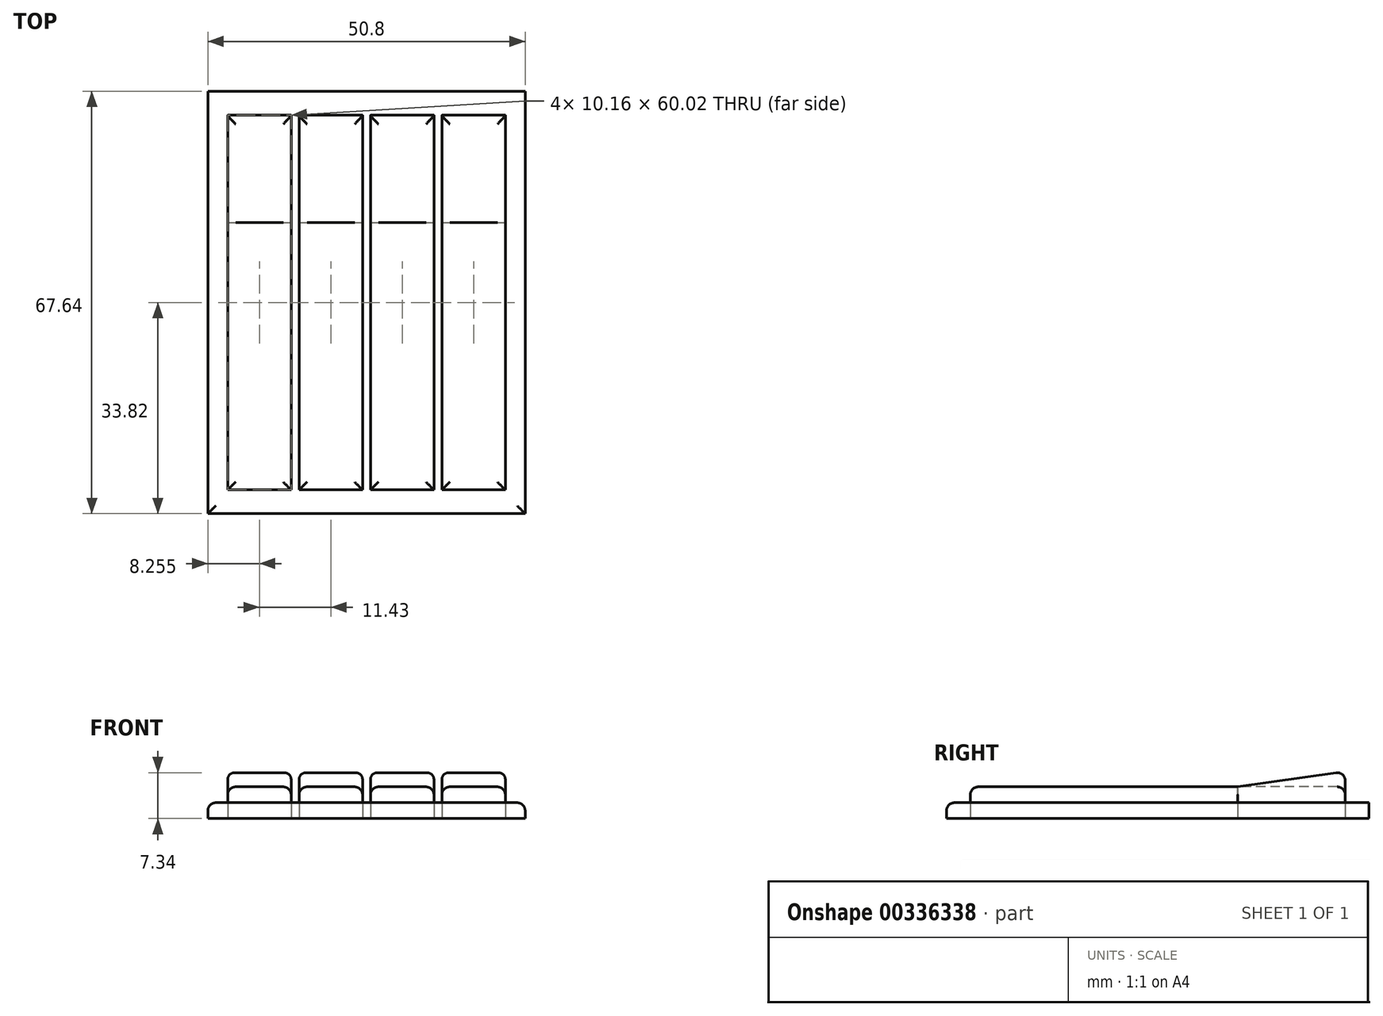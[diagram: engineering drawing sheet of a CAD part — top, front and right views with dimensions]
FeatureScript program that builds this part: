
annotation { "Feature Type Name" : "Feature", "Feature Type Description" : "" }
export const myFeature = defineFeature(function(context is Context, id is Id, definition is map)
    precondition{}
    {
        {
            var Q0;
            Q0=qCreatedBy(makeId("Top.planeOp"),FACE);
            var sketch = newSketch(context, id + "F0", { "sketchPlane" : qUnion([Q0])});
            skPoint(sketch, "E0.visualSharp", {"position": v(-51.01, 40.39) * mm});
            skPoint(sketch, "E1.visualSharp", {"position": v(51.07, 40.48) * mm});
            skPoint(sketch, "E2.visualSharp", {"position": v(0.11, -47.97) * mm});
            skLineSegment(sketch, "E3.bottom", {"start": v(25.4, 33.82) * mm, "end": v(-25.4, 33.82) * mm});
            skLineSegment(sketch, "E3.top", {"start": v(25.4, -33.82) * mm, "end": v(-25.4, -33.82) * mm});
            skLineSegment(sketch, "E3.left", {"start": v(25.4, 33.82) * mm, "end": v(25.4, -33.82) * mm});
            skLineSegment(sketch, "E3.right", {"start": v(-25.4, 33.82) * mm, "end": v(-25.4, -33.82) * mm});
            skPoint(sketch, "E3.middle", {"position": v(-17.14, 0) * mm});
            skLineSegment(sketch, "E4.bottom", {"start": v(-12.06, 30) * mm, "end": v(-22.22, 30) * mm});
            skLineSegment(sketch, "E4.top", {"start": v(-12.06, -30) * mm, "end": v(-22.22, -30) * mm});
            skLineSegment(sketch, "E4.left", {"start": v(-12.06, 30) * mm, "end": v(-12.06, -30) * mm});
            skLineSegment(sketch, "E4.right", {"start": v(-22.22, 30) * mm, "end": v(-22.22, -30) * mm});
            skPoint(sketch, "E5.1.0.0", {"position": v(-5.71, 0) * mm});
            skLineSegment(sketch, "E5.1.0.1", {"start": v(-0.63, -30) * mm, "end": v(-10.8, -30) * mm});
            skLineSegment(sketch, "E5.1.0.2", {"start": v(-0.63, 30) * mm, "end": v(-0.63, -30) * mm});
            skLineSegment(sketch, "E5.1.0.3", {"start": v(-10.8, 30) * mm, "end": v(-10.8, -30) * mm});
            skLineSegment(sketch, "E5.1.0.4", {"start": v(-0.63, 30) * mm, "end": v(-10.8, 30) * mm});
            skPoint(sketch, "E5.1.0.5", {"position": v(-5.71, 0) * mm});
            skPoint(sketch, "E5.2.0.0", {"position": v(5.72, 0) * mm});
            skLineSegment(sketch, "E5.2.0.1", {"start": v(10.8, -30) * mm, "end": v(0.64, -30) * mm});
            skLineSegment(sketch, "E5.2.0.2", {"start": v(10.8, 30) * mm, "end": v(10.8, -30) * mm});
            skLineSegment(sketch, "E5.2.0.3", {"start": v(0.64, 30) * mm, "end": v(0.64, -30) * mm});
            skLineSegment(sketch, "E5.2.0.4", {"start": v(10.8, 30) * mm, "end": v(0.64, 30) * mm});
            skPoint(sketch, "E5.2.0.5", {"position": v(5.72, 0) * mm});
            skPoint(sketch, "E5.3.0.0", {"position": v(17.15, 0) * mm});
            skLineSegment(sketch, "E5.3.0.1", {"start": v(22.23, -30) * mm, "end": v(12.07, -30) * mm});
            skLineSegment(sketch, "E5.3.0.2", {"start": v(22.23, 30) * mm, "end": v(22.23, -30) * mm});
            skLineSegment(sketch, "E5.3.0.3", {"start": v(12.07, 30) * mm, "end": v(12.07, -30) * mm});
            skLineSegment(sketch, "E5.3.0.4", {"start": v(22.23, 30) * mm, "end": v(12.07, 30) * mm});
            skPoint(sketch, "E5.3.0.5", {"position": v(17.15, 0) * mm});
            skLineSegment(sketch, "E5.direction1", {"start": v(-22.22, -30) * mm, "end": v(-10.8, -30) * mm, "construction": true});
            skLineSegment(sketch, "E6", {"start": v(-22.22, 12.8) * mm, "end": v(22.23, 12.8) * mm});
            skSolve(sketch);
        }
        {
            var Q0;
            {var subQ0=sQuery(id+"F0.wireOp",EDGE,"E4.bottom");Q0=makeQuery(id+"F0.imprint","IMPRINT",FACE,{"disambiguationData":[TD([[makeQuery(id+"F0.imprint","IMPRINT",EDGE,{"derivedFrom":subQ0}),1.0]])]});}
            var Q1;
            {var subQ0=sQuery(id+"F0.wireOp",EDGE,"E5.1.0.4");Q1=makeQuery(id+"F0.imprint","IMPRINT",FACE,{"disambiguationData":[TD([[makeQuery(id+"F0.imprint","IMPRINT",EDGE,{"derivedFrom":subQ0}),1.0]])]});}
            var Q2;
            {var subQ0=sQuery(id+"F0.wireOp",EDGE,"E5.2.0.4");Q2=makeQuery(id+"F0.imprint","IMPRINT",FACE,{"disambiguationData":[TD([[makeQuery(id+"F0.imprint","IMPRINT",EDGE,{"derivedFrom":subQ0}),1.0]])]});}
            var Q3;
            {var subQ0=sQuery(id+"F0.wireOp",EDGE,"E5.3.0.4");Q3=makeQuery(id+"F0.imprint","IMPRINT",FACE,{"disambiguationData":[TD([[makeQuery(id+"F0.imprint","IMPRINT",EDGE,{"derivedFrom":subQ0}),1.0]])]});}
            extrude(context, id + "F1", {"entities" : qUnion([Q0, Q1, Q2, Q3]), "depth" : 7.62 * mm});
        }
        {
            var Q0;
            Q0=makeQuery(id+"F0.imprint","IMPRINT",FACE,{"disambiguationData":[TD([[makeQuery(id+"F0.imprint","IMPRINT",EDGE,{"derivedFrom":sQuery(id+"F0.wireOp",EDGE,"E4.bottom")}),1.0]])]});
            var Q1;
            Q1=makeQuery(id+"F0.imprint","IMPRINT",FACE,{"disambiguationData":[TD([[makeQuery(id+"F0.imprint","IMPRINT",EDGE,{"derivedFrom":sQuery(id+"F0.wireOp",EDGE,"E5.1.0.1")}),-1.0]])]});
            var Q2;
            Q2=makeQuery(id+"F0.imprint","IMPRINT",FACE,{"disambiguationData":[TD([[makeQuery(id+"F0.imprint","IMPRINT",EDGE,{"derivedFrom":sQuery(id+"F0.wireOp",EDGE,"E5.2.0.1")}),-1.0]])]});
            var Q3;
            Q3=makeQuery(id+"F0.imprint","IMPRINT",FACE,{"disambiguationData":[TD([[makeQuery(id+"F0.imprint","IMPRINT",EDGE,{"derivedFrom":sQuery(id+"F0.wireOp",EDGE,"E5.3.0.1")}),-1.0]])]});
            var Q4;
            {var subQ0=sQuery(id+"F0.wireOp",EDGE,"E4.top");Q4=makeQuery(id+"F0.imprint","IMPRINT",FACE,{"disambiguationData":[TD([[makeQuery(id+"F0.imprint","IMPRINT",EDGE,{"derivedFrom":subQ0}),-1.0]])]});}
            var Q5;
            {var subQ0=sQuery(id+"F0.wireOp",EDGE,"E5.1.0.4");Q5=makeQuery(id+"F0.imprint","IMPRINT",FACE,{"disambiguationData":[TD([[makeQuery(id+"F0.imprint","IMPRINT",EDGE,{"derivedFrom":subQ0}),1.0]])]});}
            var Q6;
            {var subQ0=sQuery(id+"F0.wireOp",EDGE,"E5.2.0.4");Q6=makeQuery(id+"F0.imprint","IMPRINT",FACE,{"disambiguationData":[TD([[makeQuery(id+"F0.imprint","IMPRINT",EDGE,{"derivedFrom":subQ0}),1.0]])]});}
            var Q7;
            {var subQ0=sQuery(id+"F0.wireOp",EDGE,"E5.3.0.4");Q7=makeQuery(id+"F0.imprint","IMPRINT",FACE,{"disambiguationData":[TD([[makeQuery(id+"F0.imprint","IMPRINT",EDGE,{"derivedFrom":subQ0}),1.0]])]});}
            extrude(context, id + "F2", {"entities" : qUnion([Q0, Q1, Q2, Q3, Q4, Q5, Q6, Q7]), "depth" : 5.08 * mm});
        }
        {
            var Q0;
            Q0=qSketchRegion(id+"F0",true);
            extrude(context, id + "F3", {"entities" : qUnion([Q0]), "depth" : 2.54 * mm});
        }
        {
            var Q0;
            {var subQ0=sQuery(id+"F0.wireOp",EDGE,"E6");Q0=makeQuery(id+"F1.opExtrude","CAP_EDGE",EDGE,{"disambiguationData":[OSD([subQ0]),TDD([makeQuery(id+"F0.imprint","IMPRINT",EDGE,{"disambiguationData":[TD([[makeQuery(id+"F0.imprint","INTERSECT",VERTEX,{"derivedFrom":[sQuery(id+"F0.wireOp",EDGE,"E4.right"),subQ0]}),-1.0]])],"derivedFrom":subQ0})])],"isStart":false});}
            var Q1;
            {var subQ0=sQuery(id+"F0.wireOp",EDGE,"E6");Q1=makeQuery(id+"F1.opExtrude","CAP_EDGE",EDGE,{"disambiguationData":[OSD([subQ0]),TDD([makeQuery(id+"F0.imprint","IMPRINT",EDGE,{"disambiguationData":[TD([[makeQuery(id+"F0.imprint","INTERSECT",VERTEX,{"derivedFrom":[sQuery(id+"F0.wireOp",EDGE,"E5.1.0.2"),subQ0]}),1.0]])],"derivedFrom":subQ0})])],"isStart":false});}
            var Q2;
            {var subQ0=sQuery(id+"F0.wireOp",EDGE,"E6");Q2=makeQuery(id+"F1.opExtrude","CAP_EDGE",EDGE,{"disambiguationData":[OSD([subQ0]),TDD([makeQuery(id+"F0.imprint","IMPRINT",EDGE,{"disambiguationData":[TD([[makeQuery(id+"F0.imprint","INTERSECT",VERTEX,{"derivedFrom":[sQuery(id+"F0.wireOp",EDGE,"E5.2.0.2"),subQ0]}),1.0]])],"derivedFrom":subQ0})])],"isStart":false});}
            var Q3;
            {var subQ0=sQuery(id+"F0.wireOp",EDGE,"E6");Q3=makeQuery(id+"F1.opExtrude","CAP_EDGE",EDGE,{"disambiguationData":[OSD([subQ0]),TDD([makeQuery(id+"F0.imprint","IMPRINT",EDGE,{"disambiguationData":[TD([[makeQuery(id+"F0.imprint","INTERSECT",VERTEX,{"derivedFrom":[sQuery(id+"F0.wireOp",EDGE,"E5.3.0.2"),subQ0]}),1.0]])],"derivedFrom":subQ0})])],"isStart":false});}
            chamfer(context, id + "F4", {"entities" : qUnion([Q0, Q1, Q2, Q3]), "chamferType" : ChamferType.TWO_OFFSETS, "width1" : 17.78 * mm, "oppositeDirection" : false, "width2" : 2.54 * mm, "tangentPropagation" : true});
        }
        {
            var Q0;
            Q0=makeQuery(id+"F3.opExtrude","CAP_EDGE",EDGE,{"disambiguationData":[OSD([sQuery(id+"F0.wireOp",EDGE,"E3.top")])],"isStart":false});
            var Q1;
            Q1=makeQuery(id+"F3.opExtrude","CAP_EDGE",EDGE,{"disambiguationData":[OSD([sQuery(id+"F0.wireOp",EDGE,"E3.right")])],"isStart":false});
            var Q2;
            Q2=makeQuery(id+"F3.opExtrude","CAP_EDGE",EDGE,{"disambiguationData":[OSD([sQuery(id+"F0.wireOp",EDGE,"E3.left")])],"isStart":false});
            fillet(context, id + "F5", {"entities" : qUnion([Q0, Q1, Q2]), "radius" : 1.27 * mm, "tangentPropagation" : true, "allowEdgeOverflow" : false});
        }
        {
            var Q0;
            Q0=makeQuery(id+"F2.opExtrude","CAP_FACE",FACE,{"disambiguationData":[OSD([sQuery(id+"F0.wireOp",EDGE,"E4.bottom"),sQuery(id+"F0.wireOp",EDGE,"E4.top"),sQuery(id+"F0.wireOp",EDGE,"E4.left"),sQuery(id+"F0.wireOp",EDGE,"E4.right")])],"isStart":false});
            var Q1;
            Q1=makeQuery(id+"F2.opExtrude","CAP_FACE",FACE,{"disambiguationData":[OSD([sQuery(id+"F0.wireOp",EDGE,"E5.1.0.1"),sQuery(id+"F0.wireOp",EDGE,"E5.1.0.2"),sQuery(id+"F0.wireOp",EDGE,"E5.1.0.3"),sQuery(id+"F0.wireOp",EDGE,"E5.1.0.4")])],"isStart":false});
            var Q2;
            Q2=makeQuery(id+"F2.opExtrude","CAP_FACE",FACE,{"disambiguationData":[OSD([sQuery(id+"F0.wireOp",EDGE,"E5.2.0.1"),sQuery(id+"F0.wireOp",EDGE,"E5.2.0.2"),sQuery(id+"F0.wireOp",EDGE,"E5.2.0.3"),sQuery(id+"F0.wireOp",EDGE,"E5.2.0.4")])],"isStart":false});
            var Q3;
            Q3=makeQuery(id+"F2.opExtrude","CAP_FACE",FACE,{"disambiguationData":[OSD([sQuery(id+"F0.wireOp",EDGE,"E5.3.0.1"),sQuery(id+"F0.wireOp",EDGE,"E5.3.0.2"),sQuery(id+"F0.wireOp",EDGE,"E5.3.0.3"),sQuery(id+"F0.wireOp",EDGE,"E5.3.0.4")])],"isStart":false});
            fillet(context, id + "F6", {"entities" : qUnion([Q0, Q1, Q2, Q3]), "radius" : 1.27 * mm, "tangentPropagation" : true, "allowEdgeOverflow" : false});
        }
        {
            var Q0;
            {var subQ0=sQuery(id+"F0.wireOp",EDGE,"E6");Q0=makeQuery(id+"F4.opChamfer","BLEND_EDGE",EDGE,{"blendedFrom":[makeQuery(id+"F1.opExtrude","CAP_EDGE",EDGE,{"disambiguationData":[OSD([subQ0]),TDD([makeQuery(id+"F0.imprint","IMPRINT",EDGE,{"disambiguationData":[TD([[makeQuery(id+"F0.imprint","INTERSECT",VERTEX,{"derivedFrom":[sQuery(id+"F0.wireOp",EDGE,"E4.right"),subQ0]}),-1.0]])],"derivedFrom":subQ0})])],"isStart":false}),makeQuery(id+"F1.opExtrude","SWEPT_FACE",FACE,{"disambiguationData":[OSD([sQuery(id+"F0.wireOp",EDGE,"E4.bottom")])]})],"blendedInto":[makeQuery(id+"F1.opExtrude","SWEPT_FACE",FACE,{"disambiguationData":[OSD([sQuery(id+"F0.wireOp",EDGE,"E4.bottom")])]})]});}
            var Q1;
            {var subQ0=sQuery(id+"F0.wireOp",EDGE,"E4.right");var subQ1=sQuery(id+"F0.wireOp",EDGE,"E6");Q1=makeQuery(id+"F4.opChamfer","BLEND_EDGE",EDGE,{"blendedFrom":[makeQuery(id+"F1.opExtrude","CAP_EDGE",EDGE,{"disambiguationData":[OSD([subQ1]),TDD([makeQuery(id+"F0.imprint","IMPRINT",EDGE,{"disambiguationData":[TD([[makeQuery(id+"F0.imprint","INTERSECT",VERTEX,{"derivedFrom":[subQ0,subQ1]}),-1.0]])],"derivedFrom":subQ1})])],"isStart":false}),makeQuery(id+"F1.opExtrude","SWEPT_FACE",FACE,{"disambiguationData":[OSD([subQ0])]})],"blendedInto":[makeQuery(id+"F1.opExtrude","SWEPT_FACE",FACE,{"disambiguationData":[OSD([subQ0])]})]});}
            var Q2;
            {var subQ0=sQuery(id+"F0.wireOp",EDGE,"E4.left");var subQ1=sQuery(id+"F0.wireOp",EDGE,"E6");Q2=makeQuery(id+"F4.opChamfer","BLEND_EDGE",EDGE,{"blendedFrom":[makeQuery(id+"F1.opExtrude","CAP_EDGE",EDGE,{"disambiguationData":[OSD([subQ1]),TDD([makeQuery(id+"F0.imprint","IMPRINT",EDGE,{"disambiguationData":[TD([[makeQuery(id+"F0.imprint","INTERSECT",VERTEX,{"derivedFrom":[sQuery(id+"F0.wireOp",EDGE,"E4.right"),subQ1]}),-1.0]])],"derivedFrom":subQ1})])],"isStart":false}),makeQuery(id+"F1.opExtrude","SWEPT_FACE",FACE,{"disambiguationData":[OSD([subQ0])]})],"blendedInto":[makeQuery(id+"F1.opExtrude","SWEPT_FACE",FACE,{"disambiguationData":[OSD([subQ0])]})]});}
            var Q3;
            {var subQ0=sQuery(id+"F0.wireOp",EDGE,"E5.1.0.3");var subQ1=sQuery(id+"F0.wireOp",EDGE,"E6");Q3=makeQuery(id+"F4.opChamfer","BLEND_EDGE",EDGE,{"blendedFrom":[makeQuery(id+"F1.opExtrude","CAP_EDGE",EDGE,{"disambiguationData":[OSD([subQ1]),TDD([makeQuery(id+"F0.imprint","IMPRINT",EDGE,{"disambiguationData":[TD([[makeQuery(id+"F0.imprint","INTERSECT",VERTEX,{"derivedFrom":[sQuery(id+"F0.wireOp",EDGE,"E5.1.0.2"),subQ1]}),1.0]])],"derivedFrom":subQ1})])],"isStart":false}),makeQuery(id+"F1.opExtrude","SWEPT_FACE",FACE,{"disambiguationData":[OSD([subQ0])]})],"blendedInto":[makeQuery(id+"F1.opExtrude","SWEPT_FACE",FACE,{"disambiguationData":[OSD([subQ0])]})]});}
            var Q4;
            {var subQ0=sQuery(id+"F0.wireOp",EDGE,"E6");Q4=makeQuery(id+"F4.opChamfer","BLEND_EDGE",EDGE,{"blendedFrom":[makeQuery(id+"F1.opExtrude","CAP_EDGE",EDGE,{"disambiguationData":[OSD([subQ0]),TDD([makeQuery(id+"F0.imprint","IMPRINT",EDGE,{"disambiguationData":[TD([[makeQuery(id+"F0.imprint","INTERSECT",VERTEX,{"derivedFrom":[sQuery(id+"F0.wireOp",EDGE,"E5.1.0.2"),subQ0]}),1.0]])],"derivedFrom":subQ0})])],"isStart":false}),makeQuery(id+"F1.opExtrude","SWEPT_FACE",FACE,{"disambiguationData":[OSD([sQuery(id+"F0.wireOp",EDGE,"E5.1.0.4")])]})],"blendedInto":[makeQuery(id+"F1.opExtrude","SWEPT_FACE",FACE,{"disambiguationData":[OSD([sQuery(id+"F0.wireOp",EDGE,"E5.1.0.4")])]})]});}
            var Q5;
            {var subQ0=sQuery(id+"F0.wireOp",EDGE,"E5.1.0.2");var subQ1=sQuery(id+"F0.wireOp",EDGE,"E6");Q5=makeQuery(id+"F4.opChamfer","BLEND_EDGE",EDGE,{"blendedFrom":[makeQuery(id+"F1.opExtrude","CAP_EDGE",EDGE,{"disambiguationData":[OSD([subQ1]),TDD([makeQuery(id+"F0.imprint","IMPRINT",EDGE,{"disambiguationData":[TD([[makeQuery(id+"F0.imprint","INTERSECT",VERTEX,{"derivedFrom":[subQ0,subQ1]}),1.0]])],"derivedFrom":subQ1})])],"isStart":false}),makeQuery(id+"F1.opExtrude","SWEPT_FACE",FACE,{"disambiguationData":[OSD([subQ0])]})],"blendedInto":[makeQuery(id+"F1.opExtrude","SWEPT_FACE",FACE,{"disambiguationData":[OSD([subQ0])]})]});}
            var Q6;
            {var subQ0=sQuery(id+"F0.wireOp",EDGE,"E5.2.0.3");var subQ1=sQuery(id+"F0.wireOp",EDGE,"E6");Q6=makeQuery(id+"F4.opChamfer","BLEND_EDGE",EDGE,{"blendedFrom":[makeQuery(id+"F1.opExtrude","CAP_EDGE",EDGE,{"disambiguationData":[OSD([subQ1]),TDD([makeQuery(id+"F0.imprint","IMPRINT",EDGE,{"disambiguationData":[TD([[makeQuery(id+"F0.imprint","INTERSECT",VERTEX,{"derivedFrom":[sQuery(id+"F0.wireOp",EDGE,"E5.2.0.2"),subQ1]}),1.0]])],"derivedFrom":subQ1})])],"isStart":false}),makeQuery(id+"F1.opExtrude","SWEPT_FACE",FACE,{"disambiguationData":[OSD([subQ0])]})],"blendedInto":[makeQuery(id+"F1.opExtrude","SWEPT_FACE",FACE,{"disambiguationData":[OSD([subQ0])]})]});}
            var Q7;
            {var subQ0=sQuery(id+"F0.wireOp",EDGE,"E6");Q7=makeQuery(id+"F4.opChamfer","BLEND_EDGE",EDGE,{"blendedFrom":[makeQuery(id+"F1.opExtrude","CAP_EDGE",EDGE,{"disambiguationData":[OSD([subQ0]),TDD([makeQuery(id+"F0.imprint","IMPRINT",EDGE,{"disambiguationData":[TD([[makeQuery(id+"F0.imprint","INTERSECT",VERTEX,{"derivedFrom":[sQuery(id+"F0.wireOp",EDGE,"E5.2.0.2"),subQ0]}),1.0]])],"derivedFrom":subQ0})])],"isStart":false}),makeQuery(id+"F1.opExtrude","SWEPT_FACE",FACE,{"disambiguationData":[OSD([sQuery(id+"F0.wireOp",EDGE,"E5.2.0.4")])]})],"blendedInto":[makeQuery(id+"F1.opExtrude","SWEPT_FACE",FACE,{"disambiguationData":[OSD([sQuery(id+"F0.wireOp",EDGE,"E5.2.0.4")])]})]});}
            var Q8;
            {var subQ0=sQuery(id+"F0.wireOp",EDGE,"E5.2.0.2");var subQ1=sQuery(id+"F0.wireOp",EDGE,"E6");Q8=makeQuery(id+"F4.opChamfer","BLEND_EDGE",EDGE,{"blendedFrom":[makeQuery(id+"F1.opExtrude","CAP_EDGE",EDGE,{"disambiguationData":[OSD([subQ1]),TDD([makeQuery(id+"F0.imprint","IMPRINT",EDGE,{"disambiguationData":[TD([[makeQuery(id+"F0.imprint","INTERSECT",VERTEX,{"derivedFrom":[subQ0,subQ1]}),1.0]])],"derivedFrom":subQ1})])],"isStart":false}),makeQuery(id+"F1.opExtrude","SWEPT_FACE",FACE,{"disambiguationData":[OSD([subQ0])]})],"blendedInto":[makeQuery(id+"F1.opExtrude","SWEPT_FACE",FACE,{"disambiguationData":[OSD([subQ0])]})]});}
            var Q9;
            {var subQ0=sQuery(id+"F0.wireOp",EDGE,"E5.3.0.3");var subQ1=sQuery(id+"F0.wireOp",EDGE,"E6");Q9=makeQuery(id+"F4.opChamfer","BLEND_EDGE",EDGE,{"blendedFrom":[makeQuery(id+"F1.opExtrude","CAP_EDGE",EDGE,{"disambiguationData":[OSD([subQ1]),TDD([makeQuery(id+"F0.imprint","IMPRINT",EDGE,{"disambiguationData":[TD([[makeQuery(id+"F0.imprint","INTERSECT",VERTEX,{"derivedFrom":[sQuery(id+"F0.wireOp",EDGE,"E5.3.0.2"),subQ1]}),1.0]])],"derivedFrom":subQ1})])],"isStart":false}),makeQuery(id+"F1.opExtrude","SWEPT_FACE",FACE,{"disambiguationData":[OSD([subQ0])]})],"blendedInto":[makeQuery(id+"F1.opExtrude","SWEPT_FACE",FACE,{"disambiguationData":[OSD([subQ0])]})]});}
            var Q10;
            {var subQ0=sQuery(id+"F0.wireOp",EDGE,"E6");Q10=makeQuery(id+"F4.opChamfer","BLEND_EDGE",EDGE,{"blendedFrom":[makeQuery(id+"F1.opExtrude","CAP_EDGE",EDGE,{"disambiguationData":[OSD([subQ0]),TDD([makeQuery(id+"F0.imprint","IMPRINT",EDGE,{"disambiguationData":[TD([[makeQuery(id+"F0.imprint","INTERSECT",VERTEX,{"derivedFrom":[sQuery(id+"F0.wireOp",EDGE,"E5.3.0.2"),subQ0]}),1.0]])],"derivedFrom":subQ0})])],"isStart":false}),makeQuery(id+"F1.opExtrude","SWEPT_FACE",FACE,{"disambiguationData":[OSD([sQuery(id+"F0.wireOp",EDGE,"E5.3.0.4")])]})],"blendedInto":[makeQuery(id+"F1.opExtrude","SWEPT_FACE",FACE,{"disambiguationData":[OSD([sQuery(id+"F0.wireOp",EDGE,"E5.3.0.4")])]})]});}
            var Q11;
            {var subQ0=sQuery(id+"F0.wireOp",EDGE,"E5.3.0.2");var subQ1=sQuery(id+"F0.wireOp",EDGE,"E6");Q11=makeQuery(id+"F4.opChamfer","BLEND_EDGE",EDGE,{"blendedFrom":[makeQuery(id+"F1.opExtrude","CAP_EDGE",EDGE,{"disambiguationData":[OSD([subQ1]),TDD([makeQuery(id+"F0.imprint","IMPRINT",EDGE,{"disambiguationData":[TD([[makeQuery(id+"F0.imprint","INTERSECT",VERTEX,{"derivedFrom":[subQ0,subQ1]}),1.0]])],"derivedFrom":subQ1})])],"isStart":false}),makeQuery(id+"F1.opExtrude","SWEPT_FACE",FACE,{"disambiguationData":[OSD([subQ0])]})],"blendedInto":[makeQuery(id+"F1.opExtrude","SWEPT_FACE",FACE,{"disambiguationData":[OSD([subQ0])]})]});}
            fillet(context, id + "F7", {"entities" : qUnion([Q0, Q1, Q2, Q3, Q4, Q5, Q6, Q7, Q8, Q9, Q10, Q11]), "radius" : 1.27 * mm, "tangentPropagation" : true, "allowEdgeOverflow" : false});
        }
    });
